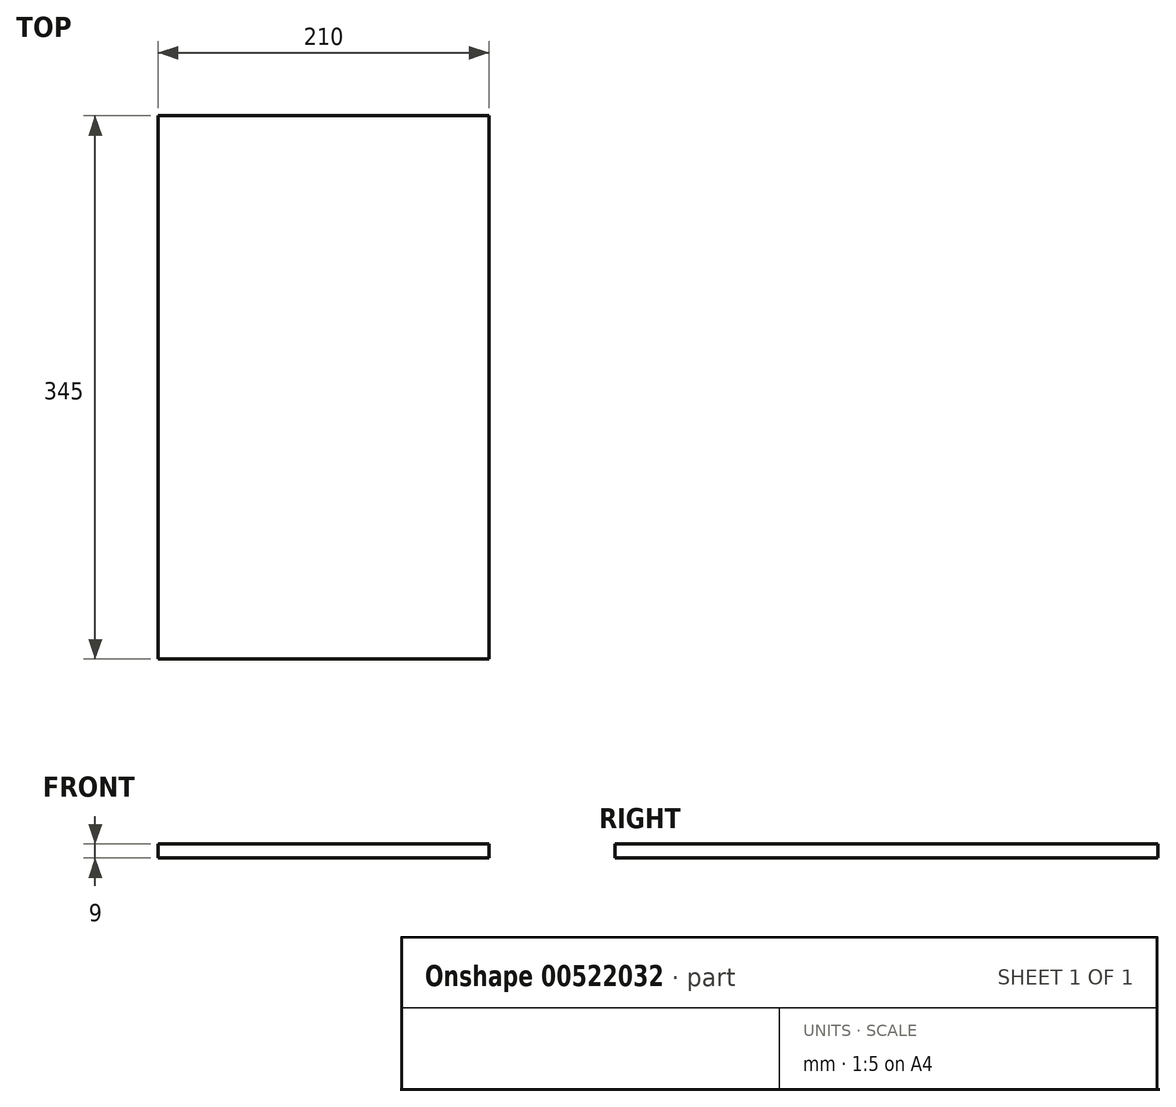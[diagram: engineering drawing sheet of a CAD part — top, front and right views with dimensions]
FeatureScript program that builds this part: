
annotation { "Feature Type Name" : "Feature", "Feature Type Description" : "" }
export const myFeature = defineFeature(function(context is Context, id is Id, definition is map)
    precondition{}
    {
        {
            var Q0;
            Q0=qCreatedBy(makeId("Top.planeOp"),FACE);
            var sketch = newSketch(context, id + "F0", { "sketchPlane" : qUnion([Q0])});
            skLineSegment(sketch, "E0.bottom", {"start": v(0, 0) * mm, "end": v(210, 0) * mm});
            skLineSegment(sketch, "E0.top", {"start": v(0, 345) * mm, "end": v(210, 345) * mm});
            skLineSegment(sketch, "E0.left", {"start": v(0, 0) * mm, "end": v(0, 345) * mm});
            skLineSegment(sketch, "E0.right", {"start": v(210, 0) * mm, "end": v(210, 345) * mm});
            skSolve(sketch);
        }
        {
            var Q0;
            Q0=makeQuery(id+"F0.imprint","IMPRINT",FACE,{"disambiguationData":[TD([[makeQuery(id+"F0.imprint","IMPRINT",EDGE,{"derivedFrom":sQuery(id+"F0.wireOp",EDGE,"E0.bottom")}),1.0]])]});
            extrude(context, id + "F1", {"entities" : qUnion([Q0]), "depth" : 9 * mm, "offsetDistance" : 25 * mm});
        }
    });
